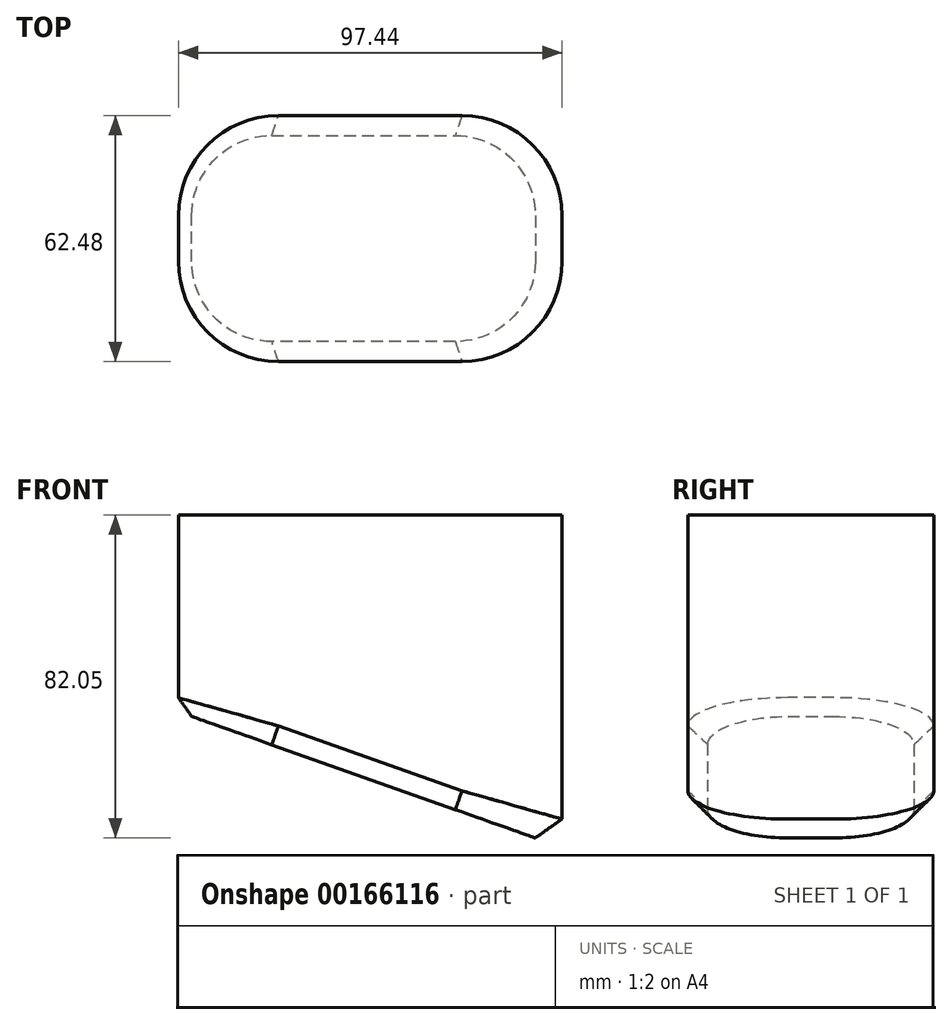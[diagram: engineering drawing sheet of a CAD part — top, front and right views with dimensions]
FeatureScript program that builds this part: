
annotation { "Feature Type Name" : "Feature", "Feature Type Description" : "" }
export const myFeature = defineFeature(function(context is Context, id is Id, definition is map)
    precondition{}
    {
        {
            var Q0;
            Q0=qCreatedBy(makeId("Front.planeOp"),FACE);
            var sketch = newSketch(context, id + "F0", { "sketchPlane" : qUnion([Q0])});
            skLineSegment(sketch, "E0", {"start": v(-57.25, 50) * mm, "end": v(40.2, 50) * mm});
            skLineSegment(sketch, "E1", {"start": v(40.2, 50) * mm, "end": v(40.2, -34.45) * mm});
            skLineSegment(sketch, "E2", {"start": v(40.2, -34.45) * mm, "end": v(-57.25, 0) * mm});
            skLineSegment(sketch, "E3", {"start": v(-57.25, 0) * mm, "end": v(-57.25, 50) * mm});
            skSolve(sketch);
        }
        {
            var Q0;
            Q0 = qSketchRegion(id + "F0", true);
            extrude(context, id + "F1", {"entities" : qUnion([Q0]), "depth" : 37.08 * mm, "hasSecondDirection" : true, "secondDirectionOppositeDirection" : true, "secondDirectionDepth" : 25.4 * mm});
        }
        {
            var Q0;
            Q0=makeQuery(id+"F1.opExtrude","CAP_EDGE",EDGE,{"disambiguationData":[OSD([sQuery(id+"F0.wireOp",EDGE,"E3")])],"isStart":false});
            var Q1;
            Q1=makeQuery(id+"F1.opExtrude","CAP_EDGE",EDGE,{"disambiguationData":[OSD([sQuery(id+"F0.wireOp",EDGE,"E3")])],"isStart":true});
            var Q2;
            Q2=makeQuery(id+"F1.opExtrude","CAP_EDGE",EDGE,{"disambiguationData":[OSD([sQuery(id+"F0.wireOp",EDGE,"E1")])],"isStart":true});
            var Q3;
            Q3=makeQuery(id+"F1.opExtrude","CAP_EDGE",EDGE,{"disambiguationData":[OSD([sQuery(id+"F0.wireOp",EDGE,"E1")])],"isStart":false});
            fillet(context, id + "F2", {"entities" : qUnion([Q0, Q1, Q2, Q3]), "radius" : 25.4 * mm, "tangentPropagation" : true, "allowEdgeOverflow" : false});
        }
        {
            var Q0;
            Q0=makeQuery(id+"F1.opExtrude","CAP_EDGE",EDGE,{"disambiguationData":[OSD([sQuery(id+"F0.wireOp",EDGE,"E2")])],"isStart":false});
            chamfer(context, id + "F3", {"entities" : qUnion([Q0]), "width" : 5.08 * mm, "tangentPropagation" : true});
        }
    });
